AUTODESK INVENTOR PART (.ipt)
format: ipt  version: 2022.1 (Build 261234020, 234B)  size: 312,320 bytes
history: native  units: mm
features: extrude x16, sketch x14, revolve x1, fillet x1, projected_geometry x1
ambient origin geometry x8: Origin, YZ Plane, XZ Plane, XY Plane, X Axis, Y Axis, Z Axis, Center Point
bodies: Solid1 (feature_tree)
feature tree (33):
  sketch  "Sketch1"  dims[d0=5.0mm d1=6.0mm]
  extrude  "Extrusion1"  Depth=5.0mm
  revolve  "Revolution1"  Angle=90.0deg
  extrude  "Extrusion2"  Depth=10.0mm
  extrude  "Extrusion3"  Depth=5.0mm TaperAngle=0.0deg
  extrude  "Extrusion4"  Depth=45.0mm TaperAngle=0.0deg
  extrude  "Extrusion5"  Depth=0.1mm TaperAngle=0.0deg
  extrude  "Extrusion6"  Depth=2.0mm TaperAngle=0.0deg
  extrude  "Extrusion7"  Depth=2.0mm TaperAngle=0.0deg
  extrude  "Extrusion8"  Depth=0.3mm TaperAngle=0.0deg
  extrude  "Extrusion9"  Depth=0.35mm TaperAngle=0.0deg
  sketch  "Sketch10"  dims[d31=0.35mm d32=0.0mm d33=0.35mm d34=0.0mm]
  extrude  "Extrusion10"  Depth=2.0mm
  extrude  "Extrusion11"  [1 undecoded]
  extrude  "Extrusion12"  [1 undecoded]
  extrude  "Extrusion13"  [1 undecoded]
  extrude  "Extrusion14"  [1 undecoded]
  extrude  "Extrusion15"  [1 undecoded]
  extrude  "Extrusion16"  [1 undecoded]
  fillet  "Fillet1"  [1 undecoded]
  sketch  "Sketch2"  dims[d2=15.0mm d3=0.0mm d4=90.0deg]
  sketch  "Sketch3"  dims[d5=1.1mm d6=0.0mm d7=10.0mm]
  sketch  "Sketch4"  dims[d8=10.0mm d9=0.0mm d10=5.0mm d11=0.0mm]
  sketch  "Sketch5"  dims[d12=7.9mm d13=45.0mm d14=0.0mm]
  sketch  "Sketch6"  dims[d15=0.1mm d16=0.0mm d17=0.1mm d18=0.0mm]
  sketch  "Sketch7"  dims[d19=0.1mm d20=0.0mm d21=2.0mm d22=0.0mm]
  sketch  "Sketch8"  dims[d23=2.0mm d24=0.0mm d25=2.0mm d26=0.0mm]
  sketch  "Sketch9"  dims[d27=14.7mm d28=0.0mm d29=0.3mm d30=0.0mm]
  sketch  "Sketch11"  dims[d35=0.2mm d36=0.0mm d37=2.0mm]
  sketch  "Sketch12"  dims[d38=0.872665mm]
  sketch  "Sketch13"
  sketch  "Sketch14"
  projected_geometry  "Projected Loop1"
note: 7 required parameter values undecoded (feature->parameter linkage not recoverable at this tier; creation-order binding heuristic only, values carry confidence <= 0.55)
